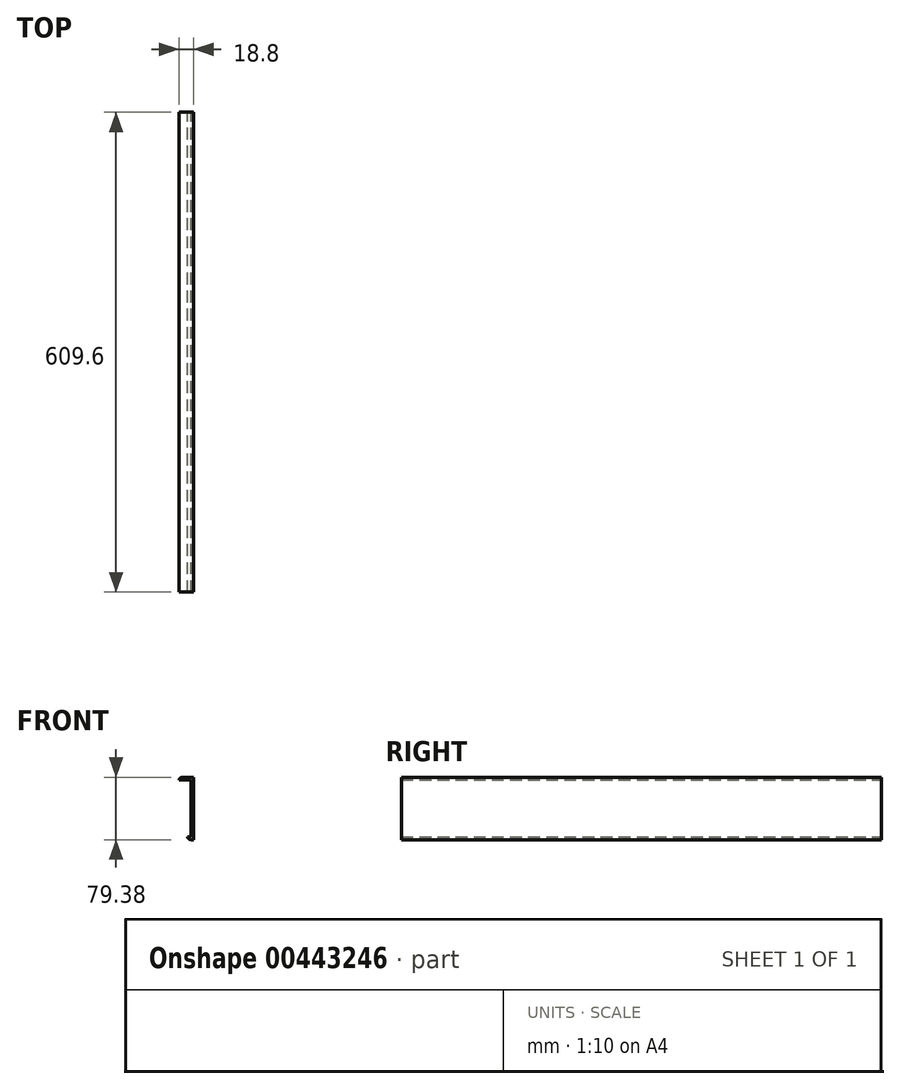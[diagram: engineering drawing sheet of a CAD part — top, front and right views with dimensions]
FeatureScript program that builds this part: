
annotation { "Feature Type Name" : "Feature", "Feature Type Description" : "" }
export const myFeature = defineFeature(function(context is Context, id is Id, definition is map)
    precondition{}
    {
        {
            var Q0;
            Q0=qCreatedBy(makeId("Front.planeOp"),FACE);
            var sketch = newSketch(context, id + "F0", { "sketchPlane" : qUnion([Q0])});
            skLineSegment(sketch, "E0.bottom", {"start": v(0, 0) * mm, "end": v(-3.56, 0) * mm});
            skLineSegment(sketch, "E0.top", {"start": v(0, 79.38) * mm, "end": v(-3.56, 79.38) * mm});
            skLineSegment(sketch, "E0.left", {"start": v(0, 0) * mm, "end": v(0, 79.38) * mm});
            skLineSegment(sketch, "E0.right", {"start": v(-3.56, 0) * mm, "end": v(-3.56, 79.38) * mm});
            skLineSegment(sketch, "E1.bottom", {"start": v(0, 79.38) * mm, "end": v(-18.8, 79.38) * mm});
            skLineSegment(sketch, "E1.top", {"start": v(0, 76.07) * mm, "end": v(-18.8, 76.07) * mm});
            skLineSegment(sketch, "E1.left", {"start": v(0, 79.38) * mm, "end": v(0, 76.07) * mm});
            skLineSegment(sketch, "E1.right", {"start": v(-18.8, 79.38) * mm, "end": v(-18.8, 76.07) * mm});
            skLineSegment(sketch, "E2.bottom", {"start": v(0, 0) * mm, "end": v(-8.13, 0) * mm});
            skLineSegment(sketch, "E2.top", {"start": v(0, 3.3) * mm, "end": v(-8.13, 3.3) * mm});
            skLineSegment(sketch, "E2.left", {"start": v(0, 0) * mm, "end": v(0, 3.3) * mm});
            skLineSegment(sketch, "E2.right", {"start": v(-8.13, 0) * mm, "end": v(-8.13, 3.3) * mm});
            skSolve(sketch);
        }
        {
            var Q0;
            Q0 = qSketchRegion(id + "F0", true);
            extrude(context, id + "F1", {"entities" : qUnion([Q0]), "depth" : 609.6 * mm});
        }
        {
            var Q0;
            Q0=makeQuery(id+"F1.opExtrude","SWEPT_EDGE",EDGE,{"disambiguationData":[OSD([sQuery(id+"F0.wireOp",EDGE,"E1.bottom"),sQuery(id+"F0.wireOp",EDGE,"E1.left")])]});
            var Q1;
            Q1=makeQuery(id+"F1.opExtrude","SWEPT_EDGE",EDGE,{"disambiguationData":[OSD([sQuery(id+"F0.wireOp",EDGE,"E2.bottom"),sQuery(id+"F0.wireOp",EDGE,"E2.left")])]});
            fillet(context, id + "F2", {"entities" : qUnion([Q0, Q1]), "radius" : 5.08 * mm, "tangentPropagation" : true, "allowEdgeOverflow" : false});
        }
    });
